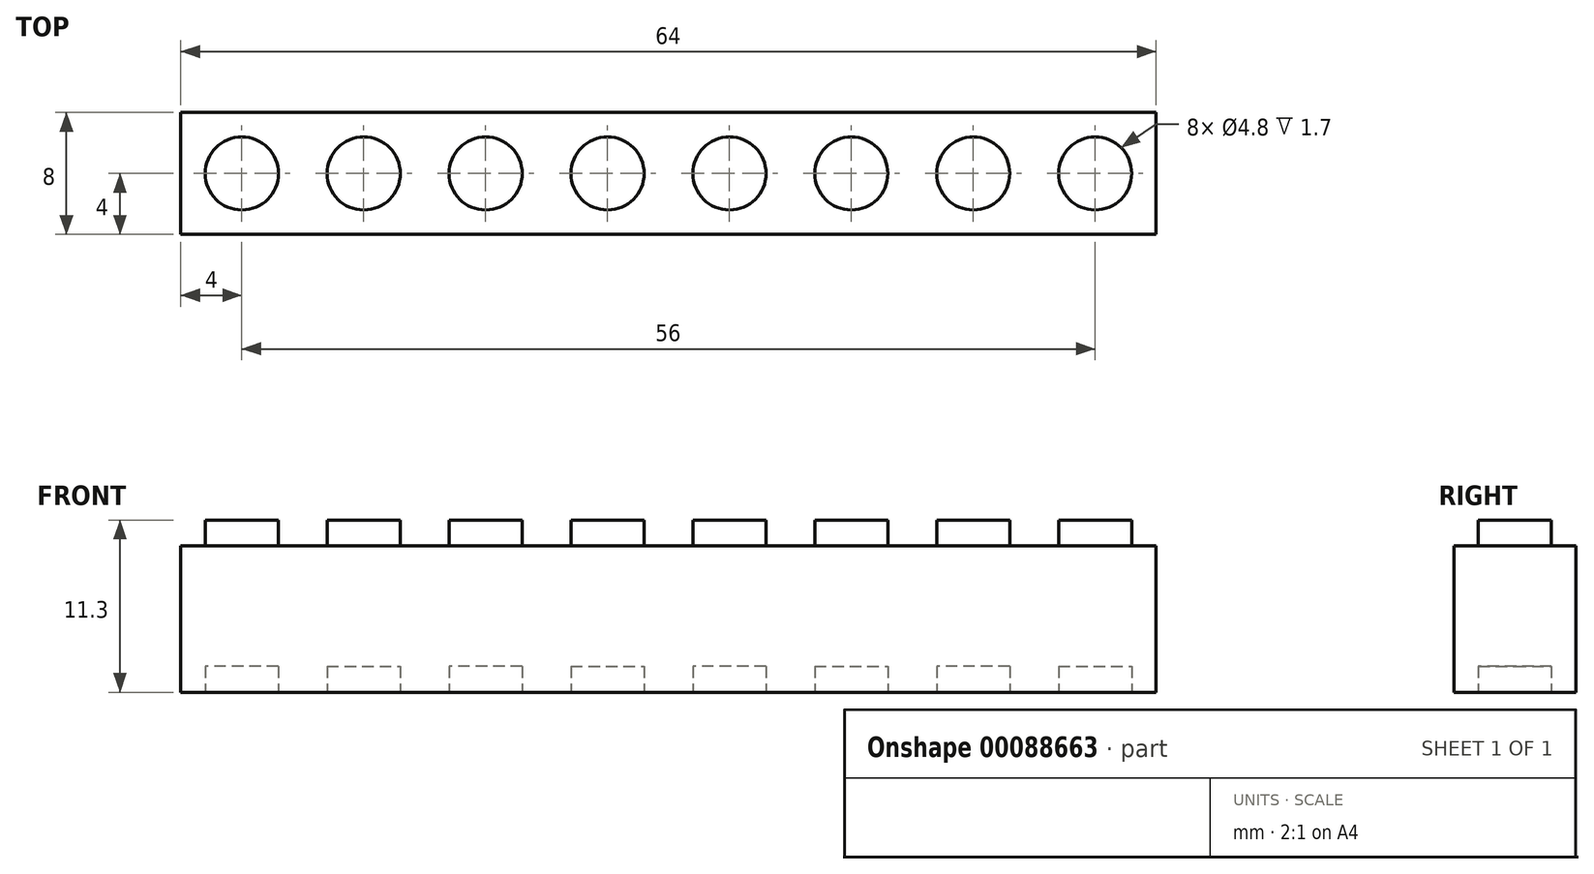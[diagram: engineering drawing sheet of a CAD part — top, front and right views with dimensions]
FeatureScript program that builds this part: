
annotation { "Feature Type Name" : "Feature", "Feature Type Description" : "" }
export const myFeature = defineFeature(function(context is Context, id is Id, definition is map)
    precondition{}
    {
        {
            var Q0;
            Q0=qCreatedBy(makeId("Front.planeOp"),FACE);
            var sketch = newSketch(context, id + "F0", { "sketchPlane" : qUnion([Q0])});
            skLineSegment(sketch, "E0.bottom", {"start": v(-4, 9.6) * mm, "end": v(-2.4, 9.6) * mm});
            skLineSegment(sketch, "E0.top", {"start": v(-4, 0) * mm, "end": v(4, 0) * mm});
            skLineSegment(sketch, "E0.left", {"start": v(-4, 9.6) * mm, "end": v(-4, 0) * mm});
            skLineSegment(sketch, "E0.right", {"start": v(4, 9.6) * mm, "end": v(4, 0) * mm});
            skLineSegment(sketch, "E1.top", {"start": v(-2.4, 11.3) * mm, "end": v(2.4, 11.3) * mm});
            skLineSegment(sketch, "E1.left", {"start": v(-2.4, 9.6) * mm, "end": v(-2.4, 11.3) * mm});
            skLineSegment(sketch, "E1.right", {"start": v(2.4, 9.6) * mm, "end": v(2.4, 11.3) * mm});
            skLineSegment(sketch, "E2", {"start": v(0, 0) * mm, "end": v(0, 24.04) * mm, "construction": true});
            skLineSegment(sketch, "E3.trimOffspring", {"start": v(2.4, 9.6) * mm, "end": v(4, 9.6) * mm});
            skSolve(sketch);
        }
        {
            var Q0;
            Q0=makeQuery(id+"F0.imprint","IMPRINT",FACE,{"disambiguationData":[TD([[makeQuery(id+"F0.imprint","IMPRINT",EDGE,{"derivedFrom":sQuery(id+"F0.wireOp",EDGE,"E0.bottom")}),-1.0]])]});
            extrude(context, id + "F1", {"entities" : qUnion([Q0]), "depth" : 8 * mm});
        }
        {
            var Q0;
            Q0=qCreatedBy(makeId("Top.planeOp"),FACE);
            var Q1;
            Q1=makeQuery(id+"F1.opExtrude","CAP_VERTEX",VERTEX,{"disambiguationData":[OSD([sQuery(id+"F0.wireOp",EDGE,"E1.top"),sQuery(id+"F0.wireOp",EDGE,"E1.right")])],"isStart":true});
            cPlane(context, id + "F2", {"entities" : qUnion([Q0, Q1]), "cplaneType" : CPlaneType.PLANE_POINT, "offset" : 152.4 * mm, "width" : 152.4 * mm, "height" : 152.4 * mm});
        }
        {
            var Q0;
            Q0=qCreatedBy(id+"F2.planeOp",FACE);
            var sketch = newSketch(context, id + "F3", { "sketchPlane" : qUnion([Q0])});
            skLineSegment(sketch, "E4.0", {"start": v(-4, -8) * mm, "end": v(-4, 0) * mm});
            skLineSegment(sketch, "E5.0", {"start": v(4, -8) * mm, "end": v(4, 0) * mm});
            skLineSegment(sketch, "E6", {"start": v(-4, 0) * mm, "end": v(4, 0) * mm});
            skLineSegment(sketch, "E7", {"start": v(-4, -8) * mm, "end": v(4, -8) * mm});
            skLineSegment(sketch, "E8", {"start": v(-4, 0) * mm, "end": v(4, -8) * mm, "construction": true});
            skLineSegment(sketch, "E9", {"start": v(-4, -8) * mm, "end": v(4, 0) * mm, "construction": true});
            skCircle(sketch, "E10", {"center": v(0, -4) * mm, "radius": 2.4 * mm});
            skSolve(sketch);
        }
        {
            var Q0;
            Q0=qSketchRegion(id+"F3",true);
            var Q1;
            Q1=makeQuery(id+"F1.opExtrude","SWEPT_FACE",FACE,{"disambiguationData":[OSD([sQuery(id+"F0.wireOp",EDGE,"E0.bottom")])]});
            extrude(context, id + "F4", {"entities" : qUnion([Q0]), "operationType" : NewBodyOperationType.REMOVE, "endBound" : BoundingType.UP_TO_SURFACE, "oppositeDirection" : true, "endBoundEntityFace" : qUnion([Q1]), "depth" : 25.4 * mm});
        }
        {
            var Q0;
            Q0=qCreatedBy(makeId("Top.planeOp"),FACE);
            var sketch = newSketch(context, id + "F5", { "sketchPlane" : qUnion([Q0])});
            skCircle(sketch, "E11.0", {"center": v(0, -4) * mm, "radius": 2.4 * mm});
            skSolve(sketch);
        }
        {
            var Q0;
            Q0=makeQuery(id+"F5.imprint","IMPRINT",FACE,{"disambiguationData":[TD([[makeQuery(id+"F5.imprint","IMPRINT",EDGE,{"derivedFrom":sQuery(id+"F5.wireOp",EDGE,"E11.0")}),1.0]])]});
            extrude(context, id + "F6", {"entities" : qUnion([Q0]), "operationType" : NewBodyOperationType.REMOVE, "depth" : 1.7 * mm});
        }
        {
            var Q0;
            Q0=qCreatedBy(makeId("Right.planeOp"),FACE);
            var Q1;
            Q1=makeQuery(id+"F1.opExtrude","CAP_VERTEX",VERTEX,{"disambiguationData":[OSD([sQuery(id+"F0.wireOp",EDGE,"E0.right"),sQuery(id+"F0.wireOp",EDGE,"E3.trimOffspring")])],"isStart":false});
            cPlane(context, id + "F7", {"entities" : qUnion([Q0, Q1]), "cplaneType" : CPlaneType.PLANE_POINT, "offset" : 152.4 * mm, "width" : 152.4 * mm, "height" : 152.4 * mm});
        }
        {
            var Q0;
            Q0=makeQuery(id+"F1.opExtrude","SWEPT_BODY",BODY,{"disambiguationData":[OSD([sQuery(id+"F0.wireOp",EDGE,"E0.bottom"),sQuery(id+"F0.wireOp",EDGE,"E0.top"),sQuery(id+"F0.wireOp",EDGE,"E0.left"),sQuery(id+"F0.wireOp",EDGE,"E0.right"),sQuery(id+"F0.wireOp",EDGE,"E1.top"),sQuery(id+"F0.wireOp",EDGE,"E1.left"),sQuery(id+"F0.wireOp",EDGE,"E1.right"),sQuery(id+"F0.wireOp",EDGE,"E3.trimOffspring")])]});
            var Q1;
            Q1=qCreatedBy(id+"F7.planeOp",FACE);
            mirror(context, id + "F8", {"operationType" : NewBodyOperationType.ADD, "entities" : qUnion([Q0]), "mirrorPlane" : qUnion([Q1])});
        }
        {
            var Q0;
            Q0=qCreatedBy(id+"F7.planeOp",FACE);
            var Q1;
            Q1=makeQuery(id+"F8.opPattern","COPY",VERTEX,{"derivedFrom":makeQuery(id+"F1.opExtrude","CAP_VERTEX",VERTEX,{"disambiguationData":[OSD([sQuery(id+"F0.wireOp",EDGE,"E0.bottom"),sQuery(id+"F0.wireOp",EDGE,"E0.left")])],"isStart":false}),"instanceName":"1"});
            cPlane(context, id + "F9", {"entities" : qUnion([Q0, Q1]), "cplaneType" : CPlaneType.PLANE_POINT, "offset" : 152.4 * mm, "width" : 152.4 * mm, "height" : 152.4 * mm});
        }
        {
            var Q0;
            Q0=makeQuery(id+"F1.opExtrude","SWEPT_BODY",BODY,{"disambiguationData":[OSD([sQuery(id+"F0.wireOp",EDGE,"E0.bottom"),sQuery(id+"F0.wireOp",EDGE,"E0.top"),sQuery(id+"F0.wireOp",EDGE,"E0.left"),sQuery(id+"F0.wireOp",EDGE,"E0.right"),sQuery(id+"F0.wireOp",EDGE,"E1.top"),sQuery(id+"F0.wireOp",EDGE,"E1.left"),sQuery(id+"F0.wireOp",EDGE,"E1.right"),sQuery(id+"F0.wireOp",EDGE,"E3.trimOffspring")])]});
            var Q1;
            Q1=qCreatedBy(id+"F9.planeOp",FACE);
            mirror(context, id + "F10", {"operationType" : NewBodyOperationType.ADD, "entities" : qUnion([Q0]), "mirrorPlane" : qUnion([Q1])});
        }
        {
            var Q0;
            Q0=qCreatedBy(makeId("Right.planeOp"),FACE);
            var Q1;
            Q1=makeQuery(id+"F10.opPattern","COPY",VERTEX,{"derivedFrom":makeQuery(id+"F1.opExtrude","CAP_VERTEX",VERTEX,{"disambiguationData":[OSD([sQuery(id+"F0.wireOp",EDGE,"E0.bottom"),sQuery(id+"F0.wireOp",EDGE,"E0.left")])],"isStart":false}),"instanceName":"1"});
            cPlane(context, id + "F11", {"entities" : qUnion([Q0, Q1]), "cplaneType" : CPlaneType.PLANE_POINT, "offset" : 152.4 * mm, "width" : 152.4 * mm, "height" : 152.4 * mm});
        }
        {
            var Q0;
            Q0=makeQuery(id+"F1.opExtrude","SWEPT_BODY",BODY,{"disambiguationData":[OSD([sQuery(id+"F0.wireOp",EDGE,"E0.bottom"),sQuery(id+"F0.wireOp",EDGE,"E0.top"),sQuery(id+"F0.wireOp",EDGE,"E0.left"),sQuery(id+"F0.wireOp",EDGE,"E0.right"),sQuery(id+"F0.wireOp",EDGE,"E1.top"),sQuery(id+"F0.wireOp",EDGE,"E1.left"),sQuery(id+"F0.wireOp",EDGE,"E1.right"),sQuery(id+"F0.wireOp",EDGE,"E3.trimOffspring")])]});
            var Q1;
            Q1=qCreatedBy(id+"F11.planeOp",FACE);
            mirror(context, id + "F12", {"operationType" : NewBodyOperationType.ADD, "entities" : qUnion([Q0]), "mirrorPlane" : qUnion([Q1])});
        }
    });
